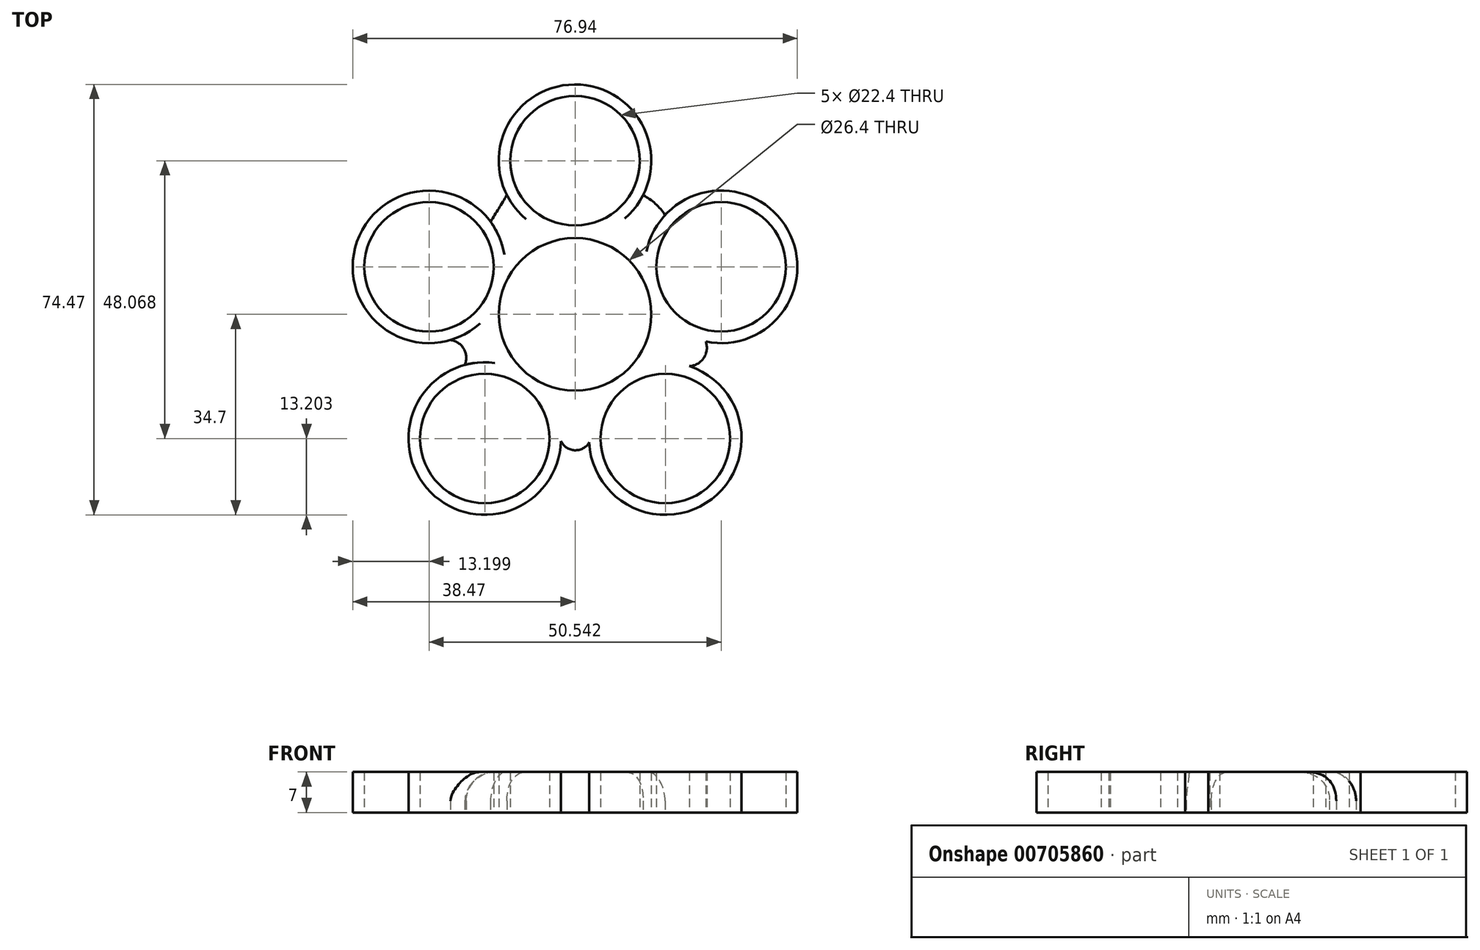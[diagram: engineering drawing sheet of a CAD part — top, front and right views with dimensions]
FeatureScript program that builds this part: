
annotation { "Feature Type Name" : "Feature", "Feature Type Description" : "" }
export const myFeature = defineFeature(function(context is Context, id is Id, definition is map)
    precondition{}
    {
        {
            var Q0;
            Q0=qCreatedBy(makeId("Top.planeOp"),FACE);
            var sketch = newSketch(context, id + "F0", { "sketchPlane" : qUnion([Q0])});
            skCircle(sketch, "E0", {"center": v(0, 0) * mm, "radius": 11.2 * mm});
            skCircle(sketch, "E1", {"center": v(0, 0) * mm, "radius": 13.2 * mm});
            skCircle(sketch, "E2", {"center": v(0, 26.57) * mm, "radius": 11.2 * mm});
            skCircle(sketch, "E3", {"center": v(0, 26.57) * mm, "radius": 13.2 * mm});
            skCircle(sketch, "E4.1.0", {"center": v(-25.27, 8.21) * mm, "radius": 11.2 * mm});
            skCircle(sketch, "E4.1.1", {"center": v(-25.27, 8.21) * mm, "radius": 13.2 * mm});
            skCircle(sketch, "E4.2.0", {"center": v(-15.62, -21.5) * mm, "radius": 11.2 * mm});
            skCircle(sketch, "E4.2.1", {"center": v(-15.62, -21.5) * mm, "radius": 13.2 * mm});
            skCircle(sketch, "E4.3.0", {"center": v(15.62, -21.5) * mm, "radius": 11.2 * mm});
            skCircle(sketch, "E4.3.1", {"center": v(15.62, -21.5) * mm, "radius": 13.2 * mm});
            skCircle(sketch, "E4.4.0", {"center": v(25.27, 8.21) * mm, "radius": 11.2 * mm});
            skCircle(sketch, "E4.4.1", {"center": v(25.27, 8.21) * mm, "radius": 13.2 * mm});
            skArc(sketch, "E5", {"start": v(-11.78, 20.62) * mm, "mid": v(-13.2, 18.32) * mm, "end": v(-14.63, 16.02) * mm});
            skArc(sketch, "E6", {"start": v(15.58, 17.18) * mm, "mid": v(13.9, 19.13) * mm, "end": v(11.78, 20.62) * mm});
            skArc(sketch, "E7", {"start": v(18.02, -8.52) * mm, "mid": v(21.65, -8.24) * mm, "end": v(22.6, -4.72) * mm});
            skArc(sketch, "E8", {"start": v(-2.43, -21.94) * mm, "mid": v(-0.07, -23.53) * mm, "end": v(2.44, -22.18) * mm});
            skArc(sketch, "E9", {"start": v(-19.06, -8.75) * mm, "mid": v(-19.25, -6) * mm, "end": v(-21.55, -4.45) * mm});
            skSolve(sketch);
        }
        {
            var Q0;
            Q0 = qSketchRegion(id + "F0", true);
            extrude(context, id + "F1", {"entities" : qUnion([Q0]), "depth" : 7 * mm, "offsetDistance" : 25 * mm});
        }
        {
            var Q0;
            Q0=makeQuery(id+"F1.opExtrude","CAP_EDGE",EDGE,{"disambiguationData":[OSD([sQuery(id+"F0.wireOp",EDGE,"E6")])],"isStart":false});
            var Q1;
            Q1=makeQuery(id+"F1.opExtrude","CAP_EDGE",EDGE,{"disambiguationData":[OSD([sQuery(id+"F0.wireOp",EDGE,"E5")])],"isStart":false});
            var Q2;
            Q2=makeQuery(id+"F1.opExtrude","CAP_EDGE",EDGE,{"disambiguationData":[OSD([sQuery(id+"F0.wireOp",EDGE,"E9")])],"isStart":false});
            fillet(context, id + "F2", {"entities" : qUnion([Q0, Q1, Q2]), "radius" : 5 * mm, "tangentPropagation" : true, "allowEdgeOverflow" : false});
        }
    });
